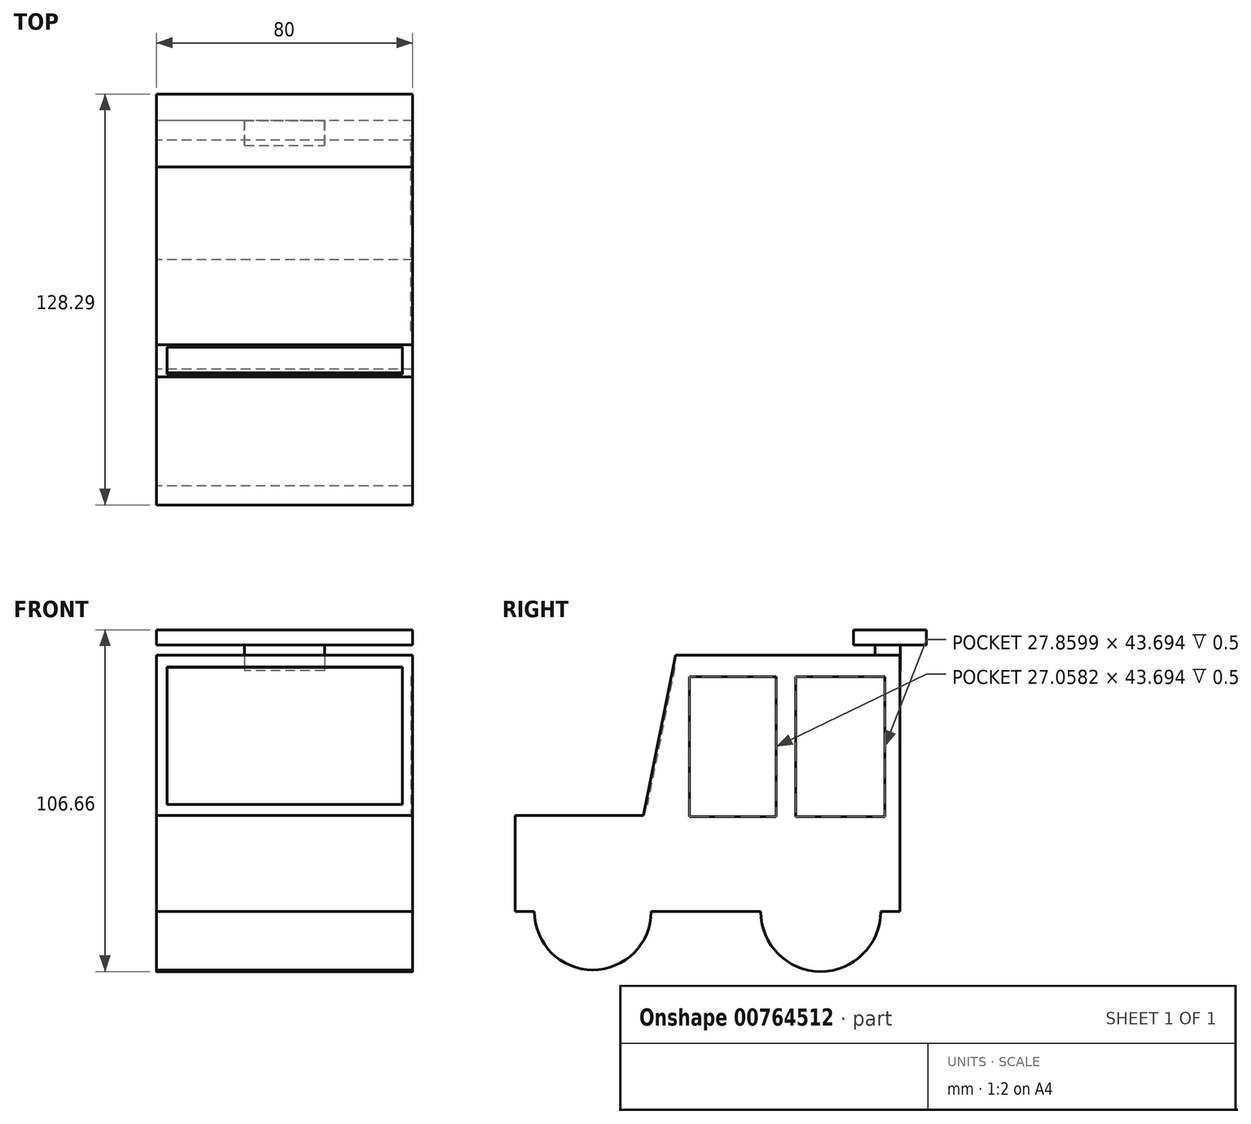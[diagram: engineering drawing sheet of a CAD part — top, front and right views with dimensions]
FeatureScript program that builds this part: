
annotation { "Feature Type Name" : "Feature", "Feature Type Description" : "" }
export const myFeature = defineFeature(function(context is Context, id is Id, definition is map)
    precondition{}
    {
        {
            var Q0;
            Q0=qCreatedBy(makeId("Right.planeOp"),FACE);
            var sketch = newSketch(context, id + "F0", { "sketchPlane" : qUnion([Q0])});
            skLineSegment(sketch, "E0", {"start": v(-85.6, 0) * mm, "end": v(-85.6, 30) * mm});
            skLineSegment(sketch, "E1", {"start": v(-85.6, 30) * mm, "end": v(-45.6, 30) * mm});
            skLineSegment(sketch, "E2", {"start": v(-35.6, 80) * mm, "end": v(34.4, 80) * mm});
            skLineSegment(sketch, "E3", {"start": v(34.4, 80) * mm, "end": v(34.4, 0) * mm});
            skLineSegment(sketch, "E4", {"start": v(34.4, 0) * mm, "end": v(-85.6, 0) * mm});
            skLineSegment(sketch, "E5", {"start": v(-45.6, 30) * mm, "end": v(-35.6, 80) * mm});
            skSolve(sketch);
        }
        {
            var Q0;
            Q0=qCreatedBy(makeId("Right.planeOp"),FACE);
            var sketch = newSketch(context, id + "F1", { "sketchPlane" : qUnion([Q0])});
            skCircle(sketch, "E6", {"center": v(-61.44, 0) * mm, "radius": 18.2 * mm});
            skCircle(sketch, "E7", {"center": v(9.63, 0) * mm, "radius": 18.7 * mm});
            skSolve(sketch);
        }
        {
            var Q0;
            Q0 = qSketchRegion(id + "F0", true);
            extrude(context, id + "F2", {"entities" : qUnion([Q0]), "endBound" : BoundingType.SYMMETRIC, "depth" : 80 * mm, "offsetDistance" : 25 * mm});
        }
        {
            var Q0;
            Q0=makeQuery(id+"F1.imprint","IMPRINT",FACE,{"disambiguationData":[TD([[makeQuery(id+"F1.imprint","IMPRINT",EDGE,{"derivedFrom":sQuery(id+"F1.wireOp",EDGE,"E6")}),1.0]])]});
            var Q1;
            Q1=makeQuery(id+"F1.imprint","IMPRINT",FACE,{"disambiguationData":[TD([[makeQuery(id+"F1.imprint","IMPRINT",EDGE,{"derivedFrom":sQuery(id+"F1.wireOp",EDGE,"Ko4uiB0i-q3tj-UFu5-7f77-qfxrTsiqLDtb")}),1.0]])]});
            var Q2;
            Q2=makeQuery(id+"F1.imprint","IMPRINT",FACE,{"disambiguationData":[TD([[makeQuery(id+"F1.imprint","IMPRINT",EDGE,{"derivedFrom":sQuery(id+"F1.wireOp",EDGE,"E7")}),1.0]])]});
            extrude(context, id + "F3", {"entities" : qUnion([Q0, Q1, Q2]), "operationType" : NewBodyOperationType.ADD, "endBound" : BoundingType.SYMMETRIC, "depth" : 80 * mm, "offsetDistance" : 25 * mm});
        }
        {
            var Q0;
            Q0=makeQuery(id+"F3.boolean.opBoolean","MERGE",FACE,{"derivedFrom":[makeQuery(id+"F2.opExtrude","CAP_FACE",FACE,{"disambiguationData":[OSD([sQuery(id+"F0.wireOp",EDGE,"E0"),sQuery(id+"F0.wireOp",EDGE,"E1"),sQuery(id+"F0.wireOp",EDGE,"E2"),sQuery(id+"F0.wireOp",EDGE,"E3"),sQuery(id+"F0.wireOp",EDGE,"E4"),sQuery(id+"F0.wireOp",EDGE,"E5")])],"isStart":false}),makeQuery(id+"F3.opExtrude","CAP_FACE",FACE,{"disambiguationData":[OSD([sQuery(id+"F1.wireOp",EDGE,"E6")])],"isStart":false}),makeQuery(id+"F3.opExtrude","CAP_FACE",FACE,{"disambiguationData":[OSD([sQuery(id+"F1.wireOp",EDGE,"E7")])],"isStart":false})]});
            var sketch = newSketch(context, id + "F4", { "sketchPlane" : qUnion([Q0])});
            skLineSegment(sketch, "E8.bottom", {"start": v(-31.26, 73.35) * mm, "end": v(-4.2, 73.35) * mm});
            skLineSegment(sketch, "E8.top", {"start": v(-31.26, 29.66) * mm, "end": v(-4.2, 29.66) * mm});
            skLineSegment(sketch, "E8.left", {"start": v(-31.26, 73.35) * mm, "end": v(-31.26, 29.66) * mm});
            skLineSegment(sketch, "E8.right", {"start": v(-4.2, 73.35) * mm, "end": v(-4.2, 29.66) * mm});
            skLineSegment(sketch, "E9.bottom", {"start": v(1.81, 73.35) * mm, "end": v(29.67, 73.35) * mm});
            skLineSegment(sketch, "E9.top", {"start": v(1.81, 29.66) * mm, "end": v(29.67, 29.66) * mm});
            skLineSegment(sketch, "E9.left", {"start": v(1.81, 73.35) * mm, "end": v(1.81, 29.66) * mm});
            skLineSegment(sketch, "E9.right", {"start": v(29.67, 73.35) * mm, "end": v(29.67, 29.66) * mm});
            skSolve(sketch);
        }
        {
            var Q0;
            Q0 = qSketchRegion(id + "F4", true);
            extrude(context, id + "F5", {"entities" : qUnion([Q0]), "operationType" : NewBodyOperationType.REMOVE, "endBound" : BoundingType.SYMMETRIC, "depth" : 1 * mm, "offsetDistance" : 25 * mm});
        }
        {
            var Q0;
            Q0=makeQuery(id+"F2.opExtrude","SWEPT_FACE",FACE,{"disambiguationData":[OSD([sQuery(id+"F0.wireOp",EDGE,"E5")])]});
            var sketch = newSketch(context, id + "F6", { "sketchPlane" : qUnion([Q0])});
            skLineSegment(sketch, "E10.bottom", {"start": v(-36.58, 67.75) * mm, "end": v(36.78, 67.75) * mm});
            skLineSegment(sketch, "E10.top", {"start": v(-36.58, 24) * mm, "end": v(36.78, 24) * mm});
            skLineSegment(sketch, "E10.left", {"start": v(-36.58, 67.75) * mm, "end": v(-36.58, 24) * mm});
            skLineSegment(sketch, "E10.right", {"start": v(36.78, 67.75) * mm, "end": v(36.78, 24) * mm});
            skSolve(sketch);
        }
        {
            var Q0;
            Q0 = qSketchRegion(id + "F6", true);
            extrude(context, id + "F7", {"entities" : qUnion([Q0]), "operationType" : NewBodyOperationType.REMOVE, "endBound" : BoundingType.SYMMETRIC, "oppositeDirection" : true, "depth" : 1 * mm, "offsetDistance" : 25 * mm});
        }
        {
            var Q0;
            Q0=qCreatedBy(makeId("Right.planeOp"),FACE);
            var sketch = newSketch(context, id + "F8", { "sketchPlane" : qUnion([Q0])});
            skPoint(sketch, "E11.right.end.orphan", {"position": v(28.98, 83.86) * mm});
            skPoint(sketch, "E12.top.end.orphan", {"position": v(32, 83.86) * mm});
            skLineSegment(sketch, "E13.bottom", {"start": v(26.6, 85.3) * mm, "end": v(34.54, 85.3) * mm});
            skLineSegment(sketch, "E13.top", {"start": v(26.6, 75.23) * mm, "end": v(34.54, 75.23) * mm});
            skLineSegment(sketch, "E13.left", {"start": v(26.6, 85.3) * mm, "end": v(26.6, 75.23) * mm});
            skLineSegment(sketch, "E13.right", {"start": v(34.54, 85.3) * mm, "end": v(34.54, 75.23) * mm});
            skSolve(sketch);
        }
        {
            var Q0;
            Q0 = qSketchRegion(id + "F8", true);
            extrude(context, id + "F9", {"entities" : qUnion([Q0]), "operationType" : NewBodyOperationType.ADD, "endBound" : BoundingType.SYMMETRIC, "depth" : 25 * mm, "offsetDistance" : 25 * mm});
        }
        {
            var Q0;
            Q0=qCreatedBy(makeId("Right.planeOp"),FACE);
            var sketch = newSketch(context, id + "F10", { "sketchPlane" : qUnion([Q0])});
            skLineSegment(sketch, "E14.bottom", {"start": v(19.88, 87.96) * mm, "end": v(42.69, 87.96) * mm});
            skLineSegment(sketch, "E14.top", {"start": v(19.88, 83.2) * mm, "end": v(42.69, 83.2) * mm});
            skLineSegment(sketch, "E14.left", {"start": v(19.88, 87.96) * mm, "end": v(19.88, 83.2) * mm});
            skLineSegment(sketch, "E14.right", {"start": v(42.69, 87.96) * mm, "end": v(42.69, 83.2) * mm});
            skSolve(sketch);
        }
        {
            var Q0;
            Q0 = qSketchRegion(id + "F10", true);
            extrude(context, id + "F11", {"entities" : qUnion([Q0]), "operationType" : NewBodyOperationType.ADD, "endBound" : BoundingType.SYMMETRIC, "depth" : 80 * mm, "offsetDistance" : 25 * mm});
        }
    });
